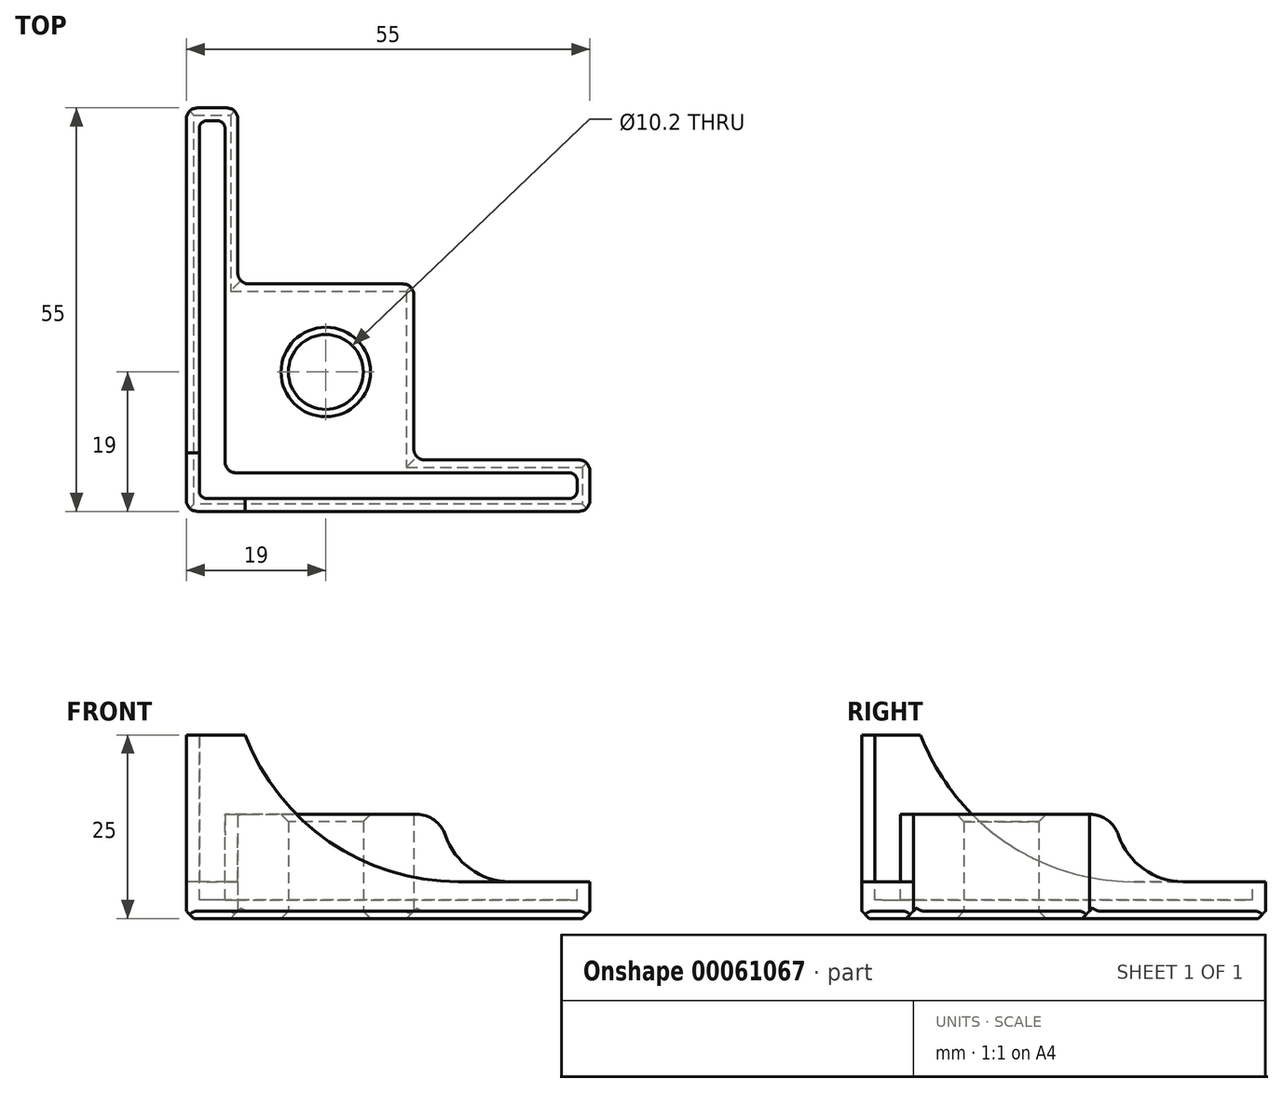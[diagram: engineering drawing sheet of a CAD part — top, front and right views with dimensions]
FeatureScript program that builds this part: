
annotation { "Feature Type Name" : "Feature", "Feature Type Description" : "" }
export const myFeature = defineFeature(function(context is Context, id is Id, definition is map)
    precondition{}
    {
        {
            var Q0;
            Q0=qCreatedBy(makeId("Top.planeOp"),FACE);
            var sketch = newSketch(context, id + "F0", { "sketchPlane" : qUnion([Q0])});
            skLineSegment(sketch, "E0", {"start": v(0, 55) * mm, "end": v(0, 0) * mm});
            skLineSegment(sketch, "E1", {"start": v(0, 0) * mm, "end": v(55, 0) * mm});
            skLineSegment(sketch, "E2", {"start": v(55, 0) * mm, "end": v(55, 7) * mm});
            skLineSegment(sketch, "E3", {"start": v(55, 7) * mm, "end": v(31, 7) * mm});
            skLineSegment(sketch, "E4", {"start": v(7, 31) * mm, "end": v(7, 55) * mm});
            skLineSegment(sketch, "E5", {"start": v(7, 55) * mm, "end": v(0, 55) * mm});
            skLineSegment(sketch, "E6.top", {"start": v(7, 31) * mm, "end": v(31, 31) * mm});
            skLineSegment(sketch, "E6.right", {"start": v(31, 7) * mm, "end": v(31, 31) * mm});
            skLineSegment(sketch, "E7", {"start": v(31, 19) * mm, "end": v(19, 19) * mm, "construction": true});
            skLineSegment(sketch, "E8", {"start": v(19, 31) * mm, "end": v(19, 19) * mm, "construction": true});
            skCircle(sketch, "E9", {"center": v(19, 19) * mm, "radius": 5.1 * mm});
            skSolve(sketch);
        }
        {
            var Q0;
            Q0 = qSketchRegion(id + "F0", true);
            extrude(context, id + "F1", {"entities" : qUnion([Q0]), "depth" : 25 * mm});
        }
        {
            var Q0;
            Q0=makeQuery(id+"F1.opExtrude","CAP_EDGE",EDGE,{"disambiguationData":[OSD([sQuery(id+"F0.wireOp",EDGE,"E6.right")])],"isStart":true});
            var Q1;
            {var subQ0=sQuery(id+"F0.wireOp",EDGE,"E6.right");var subQ1=sQuery(id+"F0.wireOp",EDGE,"E6.top");Q1=makeQuery(id+"F13.opFillet","BLEND_EDGE",EDGE,{"blendedFrom":[makeQuery(id+"F1.opExtrude","SWEPT_EDGE",EDGE,{"disambiguationData":[OSD([subQ1,subQ0])]}),makeQuery(id+"F1.opExtrude","CAP_FACE",FACE,{"disambiguationData":[OSD([sQuery(id+"F0.wireOp",EDGE,"E0"),sQuery(id+"F0.wireOp",EDGE,"E1"),sQuery(id+"F0.wireOp",EDGE,"E2"),sQuery(id+"F0.wireOp",EDGE,"E3"),sQuery(id+"F0.wireOp",EDGE,"E4"),sQuery(id+"F0.wireOp",EDGE,"E5"),subQ1,subQ0,sQuery(id+"F0.wireOp",EDGE,"E9")])],"isStart":true})],"blendedInto":[makeQuery(id+"F1.opExtrude","CAP_FACE",FACE,{"disambiguationData":[OSD([sQuery(id+"F0.wireOp",EDGE,"E0"),sQuery(id+"F0.wireOp",EDGE,"E1"),sQuery(id+"F0.wireOp",EDGE,"E2"),sQuery(id+"F0.wireOp",EDGE,"E3"),sQuery(id+"F0.wireOp",EDGE,"E4"),sQuery(id+"F0.wireOp",EDGE,"E5"),subQ1,subQ0,sQuery(id+"F0.wireOp",EDGE,"E9")])],"isStart":true})]});}
            var Q2;
            Q2=makeQuery(id+"F1.opExtrude","CAP_EDGE",EDGE,{"disambiguationData":[OSD([sQuery(id+"F0.wireOp",EDGE,"E6.top")])],"isStart":true});
            var Q3;
            Q3=makeQuery(id+"F1.opExtrude","CAP_EDGE",EDGE,{"disambiguationData":[OSD([sQuery(id+"F0.wireOp",EDGE,"E0")])],"isStart":true});
            var Q4;
            Q4=makeQuery(id+"F1.opExtrude","CAP_EDGE",EDGE,{"disambiguationData":[OSD([sQuery(id+"F0.wireOp",EDGE,"E4")])],"isStart":true});
            var Q5;
            Q5=makeQuery(id+"F1.opExtrude","CAP_EDGE",EDGE,{"disambiguationData":[OSD([sQuery(id+"F0.wireOp",EDGE,"E5")])],"isStart":true});
            var Q6;
            Q6=makeQuery(id+"F1.opExtrude","CAP_EDGE",EDGE,{"disambiguationData":[OSD([sQuery(id+"F0.wireOp",EDGE,"E1")])],"isStart":true});
            var Q7;
            Q7=makeQuery(id+"F1.opExtrude","CAP_EDGE",EDGE,{"disambiguationData":[OSD([sQuery(id+"F0.wireOp",EDGE,"E3")])],"isStart":true});
            var Q8;
            Q8=makeQuery(id+"F1.opExtrude","CAP_EDGE",EDGE,{"disambiguationData":[OSD([sQuery(id+"F0.wireOp",EDGE,"E2")])],"isStart":true});
            chamfer(context, id + "F2", {"entities" : qUnion([Q0, Q1, Q2, Q3, Q4, Q5, Q6, Q7, Q8]), "width" : 1 * mm, "tangentPropagation" : true});
        }
        {
            var Q0;
            Q0=makeQuery(id+"F1.opExtrude","CAP_FACE",FACE,{"disambiguationData":[OSD([sQuery(id+"F0.wireOp",EDGE,"E0"),sQuery(id+"F0.wireOp",EDGE,"E1"),sQuery(id+"F0.wireOp",EDGE,"E2"),sQuery(id+"F0.wireOp",EDGE,"E3"),sQuery(id+"F0.wireOp",EDGE,"E4"),sQuery(id+"F0.wireOp",EDGE,"E5"),sQuery(id+"F0.wireOp",EDGE,"E6.top"),sQuery(id+"F0.wireOp",EDGE,"E6.right"),sQuery(id+"F0.wireOp",EDGE,"E9")])],"isStart":false});
            var sketch = newSketch(context, id + "F3", { "sketchPlane" : qUnion([Q0])});
            skLineSegment(sketch, "E10", {"start": v(5.25, 53.25) * mm, "end": v(5.25, 5.25) * mm});
            skLineSegment(sketch, "E11", {"start": v(5.25, 5.25) * mm, "end": v(53.25, 5.25) * mm});
            skLineSegment(sketch, "E12", {"start": v(53.25, 1.75) * mm, "end": v(53.25, 5.25) * mm});
            skLineSegment(sketch, "E13", {"start": v(53.25, 1.75) * mm, "end": v(1.75, 1.75) * mm});
            skLineSegment(sketch, "E14", {"start": v(1.75, 1.75) * mm, "end": v(1.75, 53.25) * mm});
            skLineSegment(sketch, "E15", {"start": v(5.25, 53.25) * mm, "end": v(1.75, 53.25) * mm});
            skLineSegment(sketch, "E16", {"start": v(53.25, 3.5) * mm, "end": v(55, 3.5) * mm, "construction": true});
            skPoint(sketch, "E16.endSnap0", {"position": v(55, 3.5) * mm});
            skLineSegment(sketch, "E17", {"start": v(3.5, 55) * mm, "end": v(3.5, 53.25) * mm, "construction": true});
            skSolve(sketch);
        }
        {
            var Q0;
            Q0 = qSketchRegion(id + "F3", true);
            extrude(context, id + "F4", {"entities" : qUnion([Q0]), "operationType" : NewBodyOperationType.REMOVE, "oppositeDirection" : true, "depth" : 22.5 * mm});
        }
        {
            var Q0;
            Q0=makeQuery(id+"F1.opExtrude","CAP_FACE",FACE,{"disambiguationData":[OSD([sQuery(id+"F0.wireOp",EDGE,"E0"),sQuery(id+"F0.wireOp",EDGE,"E1"),sQuery(id+"F0.wireOp",EDGE,"E2"),sQuery(id+"F0.wireOp",EDGE,"E3"),sQuery(id+"F0.wireOp",EDGE,"E4"),sQuery(id+"F0.wireOp",EDGE,"E5"),sQuery(id+"F0.wireOp",EDGE,"E6.top"),sQuery(id+"F0.wireOp",EDGE,"E6.right"),sQuery(id+"F0.wireOp",EDGE,"E9")])],"isStart":false});
            var sketch = newSketch(context, id + "F5", { "sketchPlane" : qUnion([Q0])});
            skLineSegment(sketch, "E18.bottom", {"start": v(3.5, 3.5) * mm, "end": v(55, 3.5) * mm});
            skLineSegment(sketch, "E18.top", {"start": v(3.5, 55) * mm, "end": v(55, 55) * mm});
            skLineSegment(sketch, "E18.left", {"start": v(3.5, 3.5) * mm, "end": v(3.5, 55) * mm});
            skLineSegment(sketch, "E18.right", {"start": v(55, 3.5) * mm, "end": v(55, 55) * mm});
            skSolve(sketch);
        }
        {
            var Q0;
            Q0 = qSketchRegion(id + "F5", true);
            extrude(context, id + "F6", {"entities" : qUnion([Q0]), "operationType" : NewBodyOperationType.REMOVE, "oppositeDirection" : true, "depth" : 10.8 * mm});
        }
        {
            var Q0;
            Q0=makeQuery(id+"F1.opExtrude","SWEPT_FACE",FACE,{"disambiguationData":[OSD([sQuery(id+"F0.wireOp",EDGE,"E1")])]});
            var sketch = newSketch(context, id + "F7", { "sketchPlane" : qUnion([Q0])});
            skLineSegment(sketch, "E19.bottom", {"start": v(55, 25) * mm, "end": v(8, 25) * mm});
            skLineSegment(sketch, "E19.top", {"start": v(55, 5) * mm, "end": v(8, 5) * mm});
            skLineSegment(sketch, "E19.left", {"start": v(55, 25) * mm, "end": v(55, 5) * mm});
            skLineSegment(sketch, "E19.right", {"start": v(8, 25) * mm, "end": v(8, 5) * mm});
            skSolve(sketch);
        }
        {
            var Q0;
            Q0 = qSketchRegion(id + "F7", true);
            var Q1;
            Q1=makeQuery(id+"F4.boolean.opBoolean","COPY",FACE,{"derivedFrom":makeQuery(id+"F4.opExtrude","SWEPT_FACE",FACE,{"disambiguationData":[OSD([sQuery(id+"F3.wireOp",EDGE,"E11")])]})});
            extrude(context, id + "F8", {"entities" : qUnion([Q0]), "operationType" : NewBodyOperationType.REMOVE, "endBound" : BoundingType.UP_TO_SURFACE, "oppositeDirection" : true, "endBoundEntityFace" : qUnion([Q1]), "depth" : 25 * mm});
        }
        {
            var Q0;
            Q0=makeQuery(id+"F1.opExtrude","SWEPT_FACE",FACE,{"disambiguationData":[OSD([sQuery(id+"F0.wireOp",EDGE,"E0")])]});
            var sketch = newSketch(context, id + "F9", { "sketchPlane" : qUnion([Q0])});
            skLineSegment(sketch, "E20.bottom", {"start": v(-8, 25) * mm, "end": v(-55, 25) * mm});
            skLineSegment(sketch, "E20.top", {"start": v(-8, 5) * mm, "end": v(-55, 5) * mm});
            skLineSegment(sketch, "E20.left", {"start": v(-8, 25) * mm, "end": v(-8, 5) * mm});
            skLineSegment(sketch, "E20.right", {"start": v(-55, 25) * mm, "end": v(-55, 5) * mm});
            skSolve(sketch);
        }
        {
            var Q0;
            Q0 = qSketchRegion(id + "F9", true);
            var Q1;
            Q1=makeQuery(id+"F4.boolean.opBoolean","COPY",FACE,{"derivedFrom":makeQuery(id+"F4.opExtrude","SWEPT_FACE",FACE,{"disambiguationData":[OSD([sQuery(id+"F3.wireOp",EDGE,"E10")])]})});
            extrude(context, id + "F10", {"entities" : qUnion([Q0]), "operationType" : NewBodyOperationType.REMOVE, "endBound" : BoundingType.UP_TO_SURFACE, "oppositeDirection" : true, "endBoundEntityFace" : qUnion([Q1]), "depth" : 25 * mm});
        }
        {
            var Q0;
            Q0=makeQuery(id+"F10.boolean.opBoolean","COPY",EDGE,{"derivedFrom":makeQuery(id+"F10.opExtrude","SWEPT_EDGE",EDGE,{"disambiguationData":[OSD([sQuery(id+"F9.wireOp",EDGE,"E20.top"),sQuery(id+"F9.wireOp",EDGE,"E20.left")])]})});
            var Q1;
            Q1=makeQuery(id+"F8.boolean.opBoolean","COPY",EDGE,{"derivedFrom":makeQuery(id+"F8.opExtrude","SWEPT_EDGE",EDGE,{"disambiguationData":[OSD([sQuery(id+"F7.wireOp",EDGE,"E19.top"),sQuery(id+"F7.wireOp",EDGE,"E19.right")])]})});
            fillet(context, id + "F11", {"entities" : qUnion([Q0, Q1]), "radius" : 31.16 * mm, "tangentPropagation" : true, "allowEdgeOverflow" : false});
        }
        {
            var Q0;
            Q0=makeQuery(id+"F6.boolean.opBoolean","INTERSECT",EDGE,{"derivedFrom":[makeQuery(id+"F1.opExtrude","SWEPT_FACE",FACE,{"disambiguationData":[OSD([sQuery(id+"F0.wireOp",EDGE,"E9")])]}),makeQuery(id+"F6.opExtrude","CAP_FACE",FACE,{"disambiguationData":[OSD([sQuery(id+"F5.wireOp",EDGE,"E18.bottom"),sQuery(id+"F5.wireOp",EDGE,"E18.top"),sQuery(id+"F5.wireOp",EDGE,"E18.left"),sQuery(id+"F5.wireOp",EDGE,"E18.right")])],"isStart":false})]});
            var Q1;
            Q1=makeQuery(id+"F1.opExtrude","CAP_EDGE",EDGE,{"disambiguationData":[OSD([sQuery(id+"F0.wireOp",EDGE,"E9")])],"isStart":true});
            chamfer(context, id + "F12", {"entities" : qUnion([Q0, Q1]), "width" : 1 * mm, "tangentPropagation" : true});
        }
        {
            var Q0;
            Q0=makeQuery(id+"F1.opExtrude","SWEPT_EDGE",EDGE,{"disambiguationData":[OSD([sQuery(id+"F0.wireOp",EDGE,"E6.top"),sQuery(id+"F0.wireOp",EDGE,"E6.right")])]});
            var Q1;
            Q1=makeQuery(id+"F1.opExtrude","SWEPT_EDGE",EDGE,{"disambiguationData":[OSD([sQuery(id+"F0.wireOp",EDGE,"E3"),sQuery(id+"F0.wireOp",EDGE,"E6.right")])]});
            var Q2;
            Q2=makeQuery(id+"F1.opExtrude","SWEPT_EDGE",EDGE,{"disambiguationData":[OSD([sQuery(id+"F0.wireOp",EDGE,"E4"),sQuery(id+"F0.wireOp",EDGE,"E6.top")])]});
            var Q3;
            Q3=makeQuery(id+"F1.opExtrude","SWEPT_EDGE",EDGE,{"disambiguationData":[OSD([sQuery(id+"F0.wireOp",EDGE,"E2"),sQuery(id+"F0.wireOp",EDGE,"E3")])]});
            var Q4;
            Q4=makeQuery(id+"F1.opExtrude","SWEPT_EDGE",EDGE,{"disambiguationData":[OSD([sQuery(id+"F0.wireOp",EDGE,"E1"),sQuery(id+"F0.wireOp",EDGE,"E2")])]});
            var Q5;
            Q5=makeQuery(id+"F1.opExtrude","SWEPT_EDGE",EDGE,{"disambiguationData":[OSD([sQuery(id+"F0.wireOp",EDGE,"E0"),sQuery(id+"F0.wireOp",EDGE,"E1")])]});
            var Q6;
            Q6=makeQuery(id+"F1.opExtrude","SWEPT_EDGE",EDGE,{"disambiguationData":[OSD([sQuery(id+"F0.wireOp",EDGE,"E0"),sQuery(id+"F0.wireOp",EDGE,"E5")])]});
            var Q7;
            Q7=makeQuery(id+"F1.opExtrude","SWEPT_EDGE",EDGE,{"disambiguationData":[OSD([sQuery(id+"F0.wireOp",EDGE,"E4"),sQuery(id+"F0.wireOp",EDGE,"E5")])]});
            var Q8;
            Q8=makeQuery(id+"F4.boolean.opBoolean","COPY",EDGE,{"derivedFrom":makeQuery(id+"F4.opExtrude","SWEPT_EDGE",EDGE,{"disambiguationData":[OSD([sQuery(id+"F3.wireOp",EDGE,"E10"),sQuery(id+"F3.wireOp",EDGE,"E11")])]})});
            fillet(context, id + "F13", {"entities" : qUnion([Q0, Q1, Q2, Q3, Q4, Q5, Q6, Q7, Q8]), "radius" : 1.5 * mm, "tangentPropagation" : true, "allowEdgeOverflow" : false});
        }
        {
            var Q0;
            Q0=makeQuery(id+"F4.boolean.opBoolean","COPY",EDGE,{"derivedFrom":makeQuery(id+"F4.opExtrude","SWEPT_EDGE",EDGE,{"disambiguationData":[OSD([sQuery(id+"F3.wireOp",EDGE,"E13"),sQuery(id+"F3.wireOp",EDGE,"E14")])]})});
            var Q1;
            Q1=makeQuery(id+"F4.boolean.opBoolean","COPY",EDGE,{"derivedFrom":makeQuery(id+"F4.opExtrude","SWEPT_EDGE",EDGE,{"disambiguationData":[OSD([sQuery(id+"F3.wireOp",EDGE,"E11"),sQuery(id+"F3.wireOp",EDGE,"E12")])]})});
            var Q2;
            Q2=makeQuery(id+"F4.boolean.opBoolean","COPY",EDGE,{"derivedFrom":makeQuery(id+"F4.opExtrude","SWEPT_EDGE",EDGE,{"disambiguationData":[OSD([sQuery(id+"F3.wireOp",EDGE,"E12"),sQuery(id+"F3.wireOp",EDGE,"E13")])]})});
            var Q3;
            Q3=makeQuery(id+"F4.boolean.opBoolean","COPY",EDGE,{"derivedFrom":makeQuery(id+"F4.opExtrude","SWEPT_EDGE",EDGE,{"disambiguationData":[OSD([sQuery(id+"F3.wireOp",EDGE,"E10"),sQuery(id+"F3.wireOp",EDGE,"E15")])]})});
            var Q4;
            Q4=makeQuery(id+"F4.boolean.opBoolean","COPY",EDGE,{"derivedFrom":makeQuery(id+"F4.opExtrude","SWEPT_EDGE",EDGE,{"disambiguationData":[OSD([sQuery(id+"F3.wireOp",EDGE,"E14"),sQuery(id+"F3.wireOp",EDGE,"E15")])]})});
            fillet(context, id + "F14", {"entities" : qUnion([Q0, Q1, Q2, Q3, Q4]), "radius" : 1 * mm, "tangentPropagation" : true, "allowEdgeOverflow" : false});
        }
        {
            var Q0;
            Q0=makeQuery(id+"F8.boolean.opBoolean","MERGE",FACE,{"derivedFrom":[makeQuery(id+"F4.boolean.opBoolean","COPY",FACE,{"derivedFrom":makeQuery(id+"F4.opExtrude","SWEPT_FACE",FACE,{"disambiguationData":[OSD([sQuery(id+"F3.wireOp",EDGE,"E11")])]})}),makeQuery(id+"F8.opExtrude","CAP_FACE",FACE,{"disambiguationData":[OSD([sQuery(id+"F7.wireOp",EDGE,"E19.bottom"),sQuery(id+"F7.wireOp",EDGE,"E19.top"),sQuery(id+"F7.wireOp",EDGE,"E19.left"),sQuery(id+"F7.wireOp",EDGE,"E19.right")])],"isStart":false})]});
            var sketch = newSketch(context, id + "F15", { "sketchPlane" : qUnion([Q0])});
            skPoint(sketch, "E21.oppositeSnap0", {"position": v(53.63, 5) * mm});
            skLineSegment(sketch, "E21.bottom", {"start": v(55, 14.2) * mm, "end": v(34.83, 14.2) * mm});
            skLineSegment(sketch, "E21.top", {"start": v(55, 5) * mm, "end": v(34.83, 5) * mm});
            skLineSegment(sketch, "E21.left", {"start": v(55, 14.2) * mm, "end": v(55, 5) * mm});
            skLineSegment(sketch, "E21.right", {"start": v(34.83, 14.2) * mm, "end": v(34.83, 5) * mm});
            skSolve(sketch);
        }
        {
            var Q0;
            Q0 = qSketchRegion(id + "F15", true);
            extrude(context, id + "F16", {"entities" : qUnion([Q0]), "operationType" : NewBodyOperationType.REMOVE, "endBound" : BoundingType.THROUGH_ALL, "oppositeDirection" : true, "depth" : 25 * mm});
        }
        {
            var Q0;
            Q0=makeQuery(id+"F10.boolean.opBoolean","MERGE",FACE,{"derivedFrom":[makeQuery(id+"F4.boolean.opBoolean","COPY",FACE,{"derivedFrom":makeQuery(id+"F4.opExtrude","SWEPT_FACE",FACE,{"disambiguationData":[OSD([sQuery(id+"F3.wireOp",EDGE,"E10")])]})}),makeQuery(id+"F10.opExtrude","CAP_FACE",FACE,{"disambiguationData":[OSD([sQuery(id+"F9.wireOp",EDGE,"E20.bottom"),sQuery(id+"F9.wireOp",EDGE,"E20.top"),sQuery(id+"F9.wireOp",EDGE,"E20.left"),sQuery(id+"F9.wireOp",EDGE,"E20.right")])],"isStart":false})]});
            var sketch = newSketch(context, id + "F17", { "sketchPlane" : qUnion([Q0])});
            skLineSegment(sketch, "E22.bottom", {"start": v(-55, 14.2) * mm, "end": v(-34.5, 14.2) * mm});
            skLineSegment(sketch, "E22.top", {"start": v(-55, 5) * mm, "end": v(-34.5, 5) * mm});
            skLineSegment(sketch, "E22.left", {"start": v(-55, 14.2) * mm, "end": v(-55, 5) * mm});
            skLineSegment(sketch, "E22.right", {"start": v(-34.5, 14.2) * mm, "end": v(-34.5, 5) * mm});
            skSolve(sketch);
        }
        {
            var Q0;
            Q0 = qSketchRegion(id + "F17", true);
            extrude(context, id + "F18", {"entities" : qUnion([Q0]), "operationType" : NewBodyOperationType.REMOVE, "endBound" : BoundingType.THROUGH_ALL, "oppositeDirection" : true, "depth" : 25 * mm});
        }
        {
            var Q0;
            Q0=makeQuery(id+"F18.boolean.opBoolean","COPY",EDGE,{"derivedFrom":makeQuery(id+"F18.opExtrude","SWEPT_EDGE",EDGE,{"disambiguationData":[OSD([sQuery(id+"F17.wireOp",EDGE,"E22.top"),sQuery(id+"F17.wireOp",EDGE,"E22.right")])]})});
            var Q1;
            Q1=makeQuery(id+"F16.boolean.opBoolean","COPY",EDGE,{"derivedFrom":makeQuery(id+"F16.opExtrude","SWEPT_EDGE",EDGE,{"disambiguationData":[OSD([sQuery(id+"F15.wireOp",EDGE,"E21.top"),sQuery(id+"F15.wireOp",EDGE,"E21.right")])]})});
            fillet(context, id + "F19", {"entities" : qUnion([Q0, Q1]), "radius" : 9.3 * mm, "tangentPropagation" : true, "allowEdgeOverflow" : false});
        }
        {
            var Q0;
            Q0=makeQuery(id+"F19.opFillet","BLEND_EDGE",EDGE,{"blendedFrom":[makeQuery(id+"F16.boolean.opBoolean","COPY",EDGE,{"derivedFrom":makeQuery(id+"F16.opExtrude","SWEPT_EDGE",EDGE,{"disambiguationData":[OSD([sQuery(id+"F15.wireOp",EDGE,"E21.top"),sQuery(id+"F15.wireOp",EDGE,"E21.right")])]})}),makeQuery(id+"F6.boolean.opBoolean","COPY",FACE,{"derivedFrom":makeQuery(id+"F6.opExtrude","CAP_FACE",FACE,{"disambiguationData":[OSD([sQuery(id+"F5.wireOp",EDGE,"E18.bottom"),sQuery(id+"F5.wireOp",EDGE,"E18.top"),sQuery(id+"F5.wireOp",EDGE,"E18.left"),sQuery(id+"F5.wireOp",EDGE,"E18.right")])],"isStart":false})})],"blendedInto":[makeQuery(id+"F6.boolean.opBoolean","COPY",FACE,{"derivedFrom":makeQuery(id+"F6.opExtrude","CAP_FACE",FACE,{"disambiguationData":[OSD([sQuery(id+"F5.wireOp",EDGE,"E18.bottom"),sQuery(id+"F5.wireOp",EDGE,"E18.top"),sQuery(id+"F5.wireOp",EDGE,"E18.left"),sQuery(id+"F5.wireOp",EDGE,"E18.right")])],"isStart":false})})]});
            var Q1;
            Q1=makeQuery(id+"F19.opFillet","BLEND_EDGE",EDGE,{"blendedFrom":[makeQuery(id+"F18.boolean.opBoolean","COPY",EDGE,{"derivedFrom":makeQuery(id+"F18.opExtrude","SWEPT_EDGE",EDGE,{"disambiguationData":[OSD([sQuery(id+"F17.wireOp",EDGE,"E22.top"),sQuery(id+"F17.wireOp",EDGE,"E22.right")])]})}),makeQuery(id+"F6.boolean.opBoolean","COPY",FACE,{"derivedFrom":makeQuery(id+"F6.opExtrude","CAP_FACE",FACE,{"disambiguationData":[OSD([sQuery(id+"F5.wireOp",EDGE,"E18.bottom"),sQuery(id+"F5.wireOp",EDGE,"E18.top"),sQuery(id+"F5.wireOp",EDGE,"E18.left"),sQuery(id+"F5.wireOp",EDGE,"E18.right")])],"isStart":false})})],"blendedInto":[makeQuery(id+"F6.boolean.opBoolean","COPY",FACE,{"derivedFrom":makeQuery(id+"F6.opExtrude","CAP_FACE",FACE,{"disambiguationData":[OSD([sQuery(id+"F5.wireOp",EDGE,"E18.bottom"),sQuery(id+"F5.wireOp",EDGE,"E18.top"),sQuery(id+"F5.wireOp",EDGE,"E18.left"),sQuery(id+"F5.wireOp",EDGE,"E18.right")])],"isStart":false})})]});
            fillet(context, id + "F20", {"entities" : qUnion([Q0, Q1]), "radius" : 4.16 * mm, "tangentPropagation" : true, "allowEdgeOverflow" : false});
        }
    });
